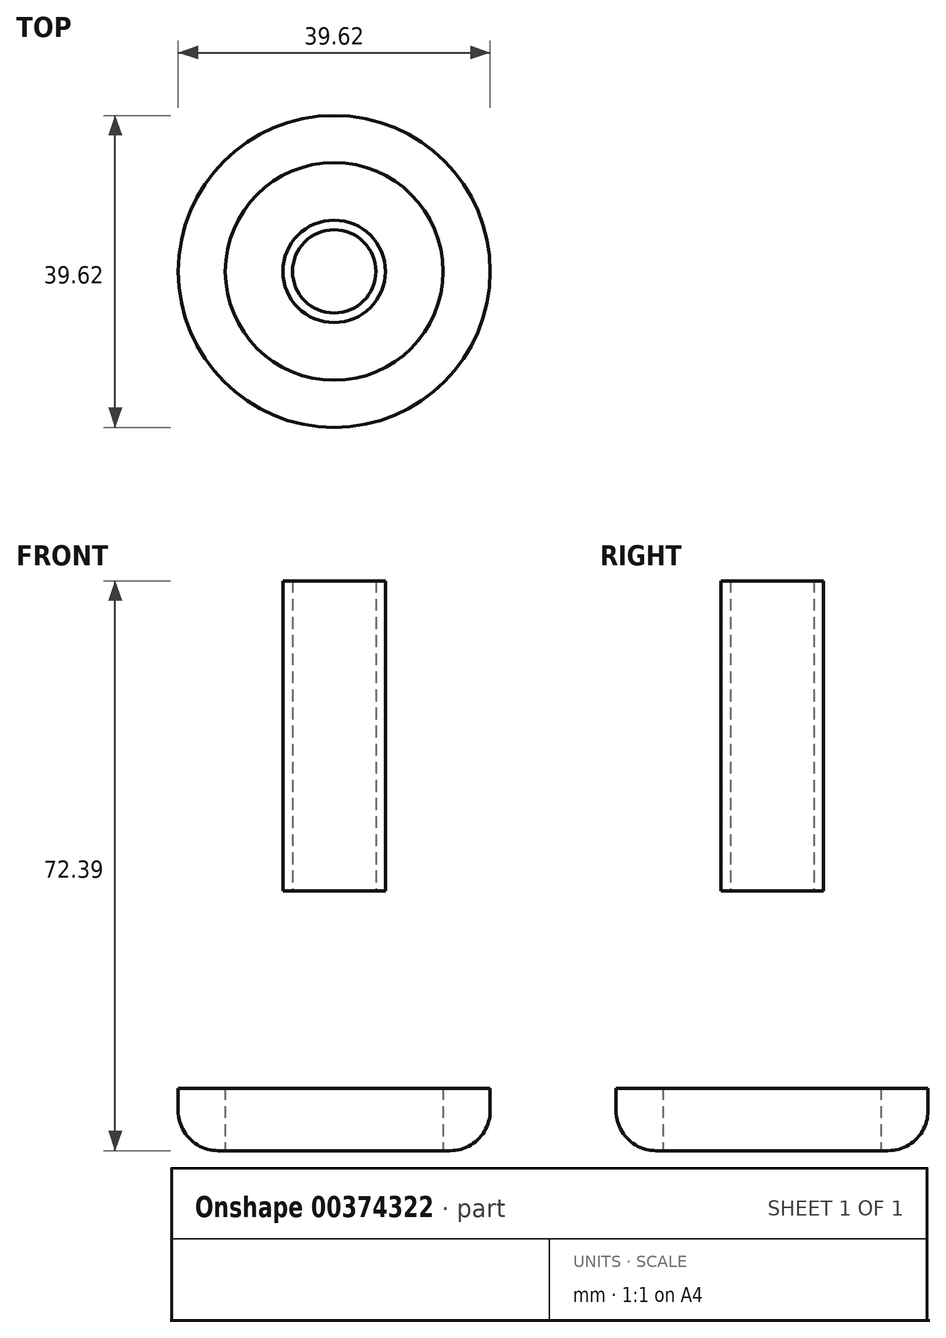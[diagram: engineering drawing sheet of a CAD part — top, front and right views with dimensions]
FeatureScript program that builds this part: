
annotation { "Feature Type Name" : "Feature", "Feature Type Description" : "" }
export const myFeature = defineFeature(function(context is Context, id is Id, definition is map)
    precondition{}
    {
        {
            var Q0;
            Q0=qCreatedBy(makeId("Top.planeOp"),FACE);
            var sketch = newSketch(context, id + "F0", { "sketchPlane" : qUnion([Q0])});
            skCircle(sketch, "E0", {"center": v(0, 0) * mm, "radius": 13.83 * mm});
            skCircle(sketch, "E1", {"center": v(0, 0) * mm, "radius": 19.81 * mm});
            skCircle(sketch, "E2", {"center": v(0, 0) * mm, "radius": 3.3 * mm});
            skPoint(sketch, "E3", {"position": v(0, 19.81) * mm});
            skLineSegment(sketch, "E4", {"start": v(0, 6.13) * mm, "end": v(0, 19.81) * mm});
            skSolve(sketch);
        }
        {
            var Q0;
            Q0 = qSketchRegion(id + "F0", true);
            extrude(context, id + "F1", {"entities" : qUnion([Q0]), "depth" : 7.94 * mm});
        }
        {
            var Q0;
            Q0=qCreatedBy(makeId("Top.planeOp"),FACE);
            cPlane(context, id + "F2", {"entities" : qUnion([Q0]), "cplaneType" : CPlaneType.OFFSET, "offset" : 33.02 * mm, "width" : 152.4 * mm, "height" : 152.4 * mm});
        }
        {
            var Q0;
            Q0=qCreatedBy(id+"F2.planeOp",FACE);
            var sketch = newSketch(context, id + "F3", { "sketchPlane" : qUnion([Q0])});
            skCircle(sketch, "E5", {"center": v(0, 0) * mm, "radius": 6.5 * mm});
            skCircle(sketch, "E6", {"center": v(0, 0) * mm, "radius": 5.3 * mm});
            skPoint(sketch, "E7", {"position": v(-3.95, 3.52) * mm});
            skLineSegment(sketch, "E8", {"start": v(0, 5.3) * mm, "end": v(0, 0) * mm});
            skSolve(sketch);
        }
        {
            var Q0;
            Q0 = qSketchRegion(id + "F3", true);
            extrude(context, id + "F4", {"entities" : qUnion([Q0]), "depth" : 39.37 * mm});
        }
        {
            var Q0;
            Q0 = qSketchRegion(id + "F3", true);
            extrude(context, id + "F5", {"entities" : qUnion([Q0]), "operationType" : NewBodyOperationType.REMOVE, "oppositeDirection" : true, "depth" : 25.4 * mm});
        }
        {
            var Q0;
            Q0=makeQuery(id+"F1.opExtrude","CAP_EDGE",EDGE,{"disambiguationData":[OSD([sQuery(id+"F0.wireOp",EDGE,"E1")])],"isStart":true});
            fillet(context, id + "F6", {"entities" : qUnion([Q0]), "radius" : 5.08 * mm, "tangentPropagation" : true, "allowEdgeOverflow" : false});
        }
        {
            var Q0;
            Q0=qCreatedBy(makeId("Top.planeOp"),FACE);
            cPlane(context, id + "F7", {"entities" : qUnion([Q0]), "cplaneType" : CPlaneType.OFFSET, "offset" : 7.94 * mm, "width" : 152.4 * mm, "height" : 152.4 * mm});
        }
        {
            var Q0;
            Q0=qCreatedBy(id+"F2.planeOp",FACE);
            var sketch = newSketch(context, id + "F8", { "sketchPlane" : qUnion([Q0])});
            skPoint(sketch, "E9", {"position": v(3.42, -5.54) * mm});
            skSolve(sketch);
        }
        {
            var Q0;
            Q0=qCreatedBy(id+"F7.planeOp",FACE);
            var sketch = newSketch(context, id + "F9", { "sketchPlane" : qUnion([Q0])});
            skPoint(sketch, "E10", {"position": v(11.98, 6.92) * mm});
            skSolve(sketch);
        }
        {
            var Q0;
            Q0=qCreatedBy(makeId("Right.planeOp"),FACE);
            var sketch = newSketch(context, id + "F10", { "sketchPlane" : qUnion([Q0])});
            skPoint(sketch, "E11", {"position": v(5.18, 33.02) * mm});
            skPoint(sketch, "E12", {"position": v(19.81, 7.94) * mm});
            skLineSegment(sketch, "E13", {"start": v(5.18, 33.02) * mm, "end": v(19.81, 7.94) * mm});
            skPoint(sketch, "E14", {"position": v(0, 33.02) * mm});
            skPoint(sketch, "E15", {"position": v(0, 7.94) * mm});
            skLineSegment(sketch, "E16", {"start": v(0, 7.94) * mm, "end": v(19.81, 7.94) * mm});
            skLineSegment(sketch, "E17", {"start": v(0, 33.02) * mm, "end": v(5.18, 33.02) * mm});
            skSolve(sketch);
        }
        {
            var Q0;
            Q0=qCreatedBy(makeId("Right.planeOp"),FACE);
            var sketch = newSketch(context, id + "F11", { "sketchPlane" : qUnion([Q0])});
            skLineSegment(sketch, "E18", {"start": v(0, 7.94) * mm, "end": v(0, 33.02) * mm});
            skSolve(sketch);
        }
        {
            var Q0;
            Q0 = qSketchRegion(id + "F10", true);
            var Q1;
            Q1 = qConstructionFilter(qBodyType(qCreatedBy(id + "F10" ,EDGE), BodyType.WIRE), ConstructionObject.NO);
            var Q2;
            Q2=sQuery(id+"F11.wireOp",EDGE,"E18");
            revolve(context, id + "F12", {"bodyType" : ToolBodyType.SURFACE, "operationType" : NewBodyOperationType.ADD, "entities" : qUnion([Q0]), "surfaceEntities" : qUnion([Q1]), "axis" : qUnion([Q2]), "revolveType" : RevolveType.FULL});
        }
    });
